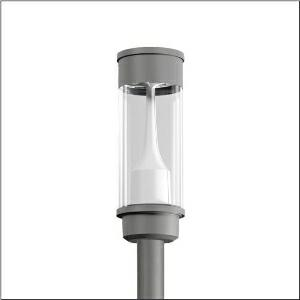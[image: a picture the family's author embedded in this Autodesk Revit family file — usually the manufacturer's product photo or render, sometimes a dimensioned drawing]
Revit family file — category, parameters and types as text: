
# Revit family: litepole_iq___st1_2a_5xa5415mf14h_d5a4
name_source: partatom
category: Lighting Fixtures
units: mm (PartAtom-declared; Revit-internal decimal feet)

## family parameters
Cut with Voids When Loaded = No
Host = Face
Light Source = No
Part Type = Normal
Room Calculation Point = No
Round Connector Dimension = Use Diameter
Shared = No

## types (1)
- --- (1 x LED, 1540 lm, 11.8 W, 2700K)
    Apparent Load = 12 VA
    CIE Flux Codes = 22 61 93 96 100
    Color Rendering = 70
    Color Temperature = 2700K
    Default Elevation = 1800 mm
    Description = Litepole iQ, mast luminaire, Module 540 iQ-SR, primary light control with 3 zone facetted reflector, of plastic, silver coated, highly specular, structured, primary optical cover: cover, of PMMA, transparent, partly coated, light distribution: ST1.2a, light emission: direct distribution, primary light characteristic: asymmetric, installation type: post-top, LED, High Power LED, rated luminous flux: 1.540lm, luminous efficacy: 131lm/W, light colour: 727, colour temperature: 2700K, control gear: iQ Street-Remote, control: optimised constant luminous flux control (CLO 2.0), Desk-Remote (wireless, voltage-free reading and setting of iQ features in the workshop via application-optimized NFC function/RFID function), Light-Fading, Smart-Wire, Night-Set, Lumen-Switch, Temp-Guard, Auto-Match, Street-Remote, pre-setting: logarithmic dimming characteristic, with terminal, 6-pole, max. 2.5mm², mains connection: 230..240V, AC, 50/60Hz, start of lifetime: 12W, end of service life: 12W, reduction: 6W, luminaire housing, upper part, of glass-fibre reinforced polyester, coated, Siteco® metallic grey (DB 702S), diameter: 210mm, height: 590mm, spigot size: d x l = 76 x 70mm (post-top) | with reducer (optional accessory) 60 x 70mm, mounting height: 3..5m, post-top mast mounting element, of diecast aluminium, coated, Siteco® metallic grey (DB 702S), Module 540 iQ-SR, traffic white (RAL 9016), equipment: standard, protection rating (complete): IP65, insulation class (complete): insulation class II (safety insulation), certification: CE, ENEC, VDE, packaging unit: 1 piece

Light Distribution: ST1.2a
    Height = 590 mm
    Lamp = 1 x LED
    Lamp Light Flux = 1540 lm
    Lamp Power = 11.8 W
    Lamp count = 1
    Length = 220 mm
    Luminous efficacy = 131 lm/W
    Manufacturer = Siteco
    ModVariant = No
    Model = 5XA5415MF14H
    Number of Poles = 1
    OnlyDefault = Yes
    Power Factor = 1
    Product Name = Litepole iQ | ST1.2a
    Product group = mast luminaire | pylon top
    ProductGroupID = 6100
    Protection Class = Protection class II
    Protection Degree = IP 65
    RLX_Detail_Level = 1
    RLX_Emergency_Light_Flux = 0 lm
    RLX_Emergency_Type = 0
    RLX_Emergency_Type_DB = No
    RlxData = <blob elided: 72057 chars, md5=0c1b859e>
    Socket = socket
    Standby Power = 0 W
    System Light Flux = 1540 lm
    System Power = 12 W
    Type Comments = factory setting: luminous flux: 100 % | dim-lin: 254 | 472 mA
    Type Image = l_1006025.jpg
    URL = http://relux.com
    VarID = @adj_152515
    Voltage = 0 V
    Weight = 0.00 kg
    Width = 0 mm  [stored 0 ft]

note: [stored X ft] marks values corroborated as IEEE doubles in the binary element streams (Revit-internal decimal feet)

## geometry (parser evidence)
native form markers: Blend x4, Sweep x12
no freeform markers — native parametric forms only
